# Revit family: Chair-Multi_Purpose-Allermuir-Casper-CS4A
name_source: partatom
category: Furniture
revit_build: Autodesk Revit MEP 2012 (Build: 20110309_2315)
units: mm (PartAtom-declared; Revit-internal decimal feet)

## types (1)
- CS4A
    04 CSI = 12 51 00
    95 CSI = 12510
    Arm = Plastic - Allermuir - Smooth Black
    Arm Height = 28 "
    Arm Rest = Plastic - Allermuir - Smooth Black
    Assembly Code = E2020200
    Base = Metal - Allermuir - Chrome - Polished
    Brochure URL = http://www.allermuir.net
    CAD Blocks URL = http://www.allermuir.net
    Color Availability = See price list for material options
    Cushion = Plastic - Allermuir - Smooth - Dark Gray
    Cushion_Visiblity = Yes
    Description = Armchair with upholstered seat pad,  4 leg frame
    Fabric Spec Sheets = http://www.allermuir.net
    Glides = Plastic - Allermuir - Smooth Black
    LEED Stats URL = http://www.allermuir.net
    Leg Material = Metal - Allermuir - Chrome - Polished
    Manufacturer = Allermuir
    Manufacturer Fax = (419) 887 5805
    Model = CS4A
    Overall Depth = 22 "
    Overall Height = 32 "
    Overall Width = 23 "
    Plastic Arms in Black = No
    Plastic glides = Yes
    Plugin Data URL = http://products.ecoscorecard.com
    Pricing URL = http://www.allermuir.net
    Product Line = Casper
    Product Page URL = http://www.allermuir.net
    Seat Depth = 18 "
    Seat Finesh = Plastic - Allermuir - Smooth - Dark Gray
    Seat Height = 19 "
    Seat Width = 18 "
    Seat or Top = Plastic - Allermuir - Smooth - Dark Gray
    Stacks = Yes
    Subcategory = Multi-Purpose Line
    Tubular Steel Legs = Yes
    URL = http://www.allermuir.net
    Upholstered Seat = No
    Weight = 15.0 lb
    ecoScorecard Product Page = http://products.ecoscorecard.com
    ecoScorecard_data = http://thesenatorgroup.ecoscorecard.com

## geometry (parser evidence)
native form markers: Blend x18, Sweep x3
no freeform markers — native parametric forms only
